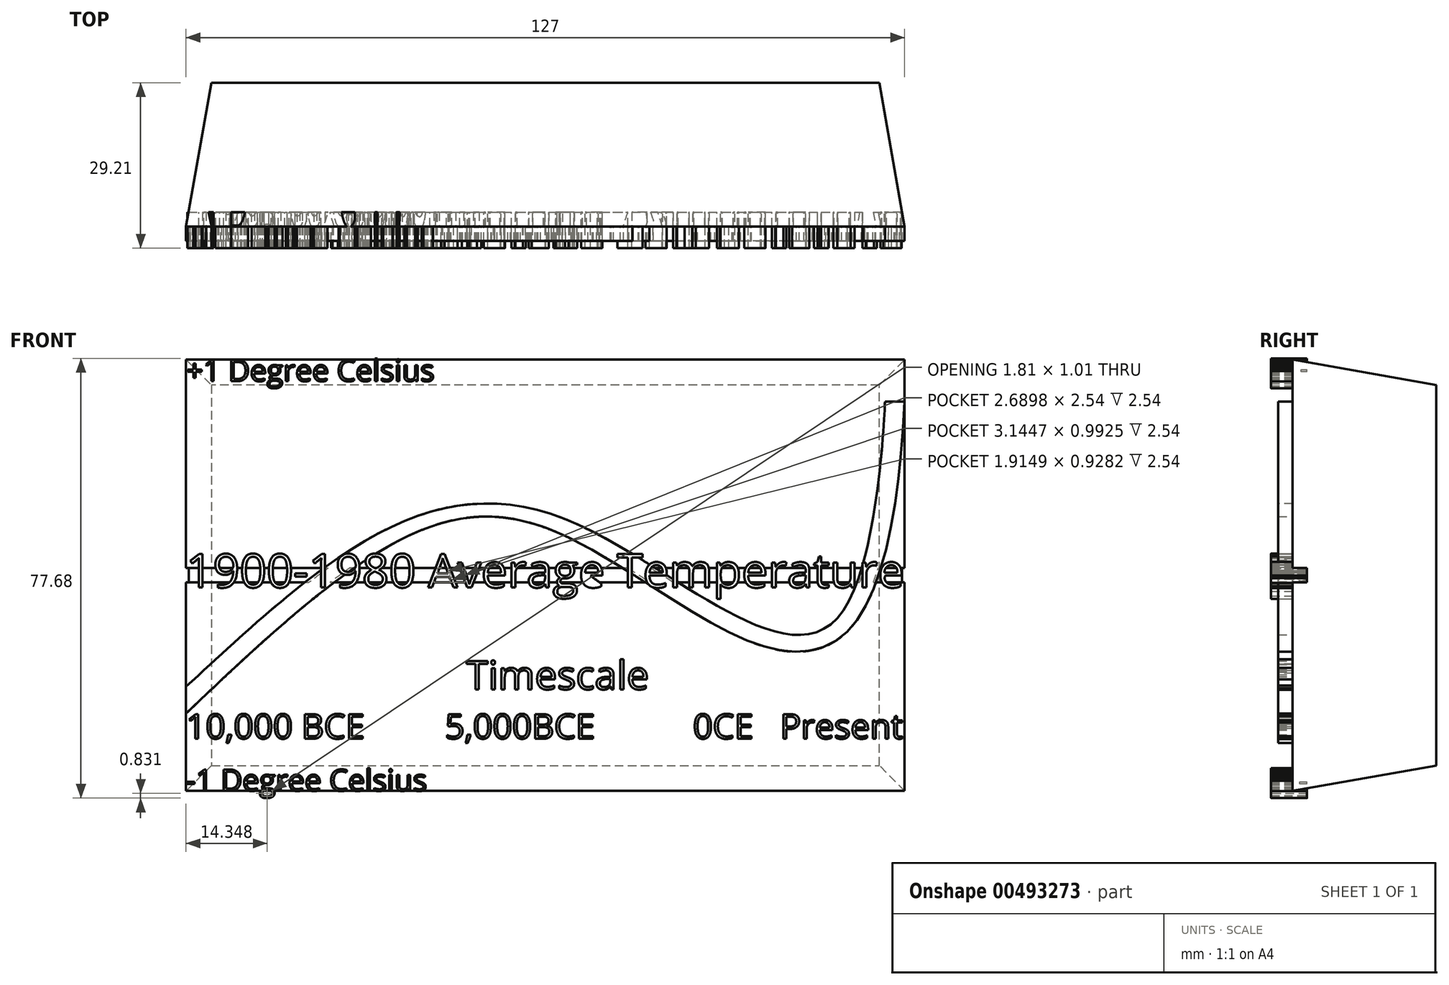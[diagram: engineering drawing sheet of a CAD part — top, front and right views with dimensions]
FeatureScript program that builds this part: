
annotation { "Feature Type Name" : "Feature", "Feature Type Description" : "" }
export const myFeature = defineFeature(function(context is Context, id is Id, definition is map)
    precondition{}
    {
        {
            var Q0;
            Q0=qCreatedBy(makeId("Front.planeOp"),FACE);
            var sketch = newSketch(context, id + "F0", { "sketchPlane" : qUnion([Q0])});
            skLineSegment(sketch, "E0.bottom", {"start": v(-127, 76.2) * mm, "end": v(0, 76.2) * mm});
            skLineSegment(sketch, "E0.top", {"start": v(-127, 0) * mm, "end": v(0, 0) * mm});
            skLineSegment(sketch, "E0.left", {"start": v(-127, 76.2) * mm, "end": v(-127, 0) * mm});
            skLineSegment(sketch, "E0.right", {"start": v(0, 76.2) * mm, "end": v(0, 0) * mm});
            skSolve(sketch);
        }
        {
            var Q0;
            Q0 = qSketchRegion(id + "F0", true);
            extrude(context, id + "F1", {"entities" : qUnion([Q0]), "oppositeDirection" : true, "depth" : 25.4 * mm, "hasDraft" : true, "draftAngle" : 10 * degree, "draftPullDirection" : true});
        }
        {
            var Q0;
            Q0=makeQuery(id+"F1.opExtrude","CAP_FACE",FACE,{"disambiguationData":[OSD([sQuery(id+"F0.wireOp",EDGE,"E0.bottom"),sQuery(id+"F0.wireOp",EDGE,"E0.top"),sQuery(id+"F0.wireOp",EDGE,"E0.left"),sQuery(id+"F0.wireOp",EDGE,"E0.right")])],"isStart":true});
            var sketch = newSketch(context, id + "F2", { "sketchPlane" : qUnion([Q0])});
            skLineSegment(sketch, "E1.bottom", {"start": v(-127, 39.37) * mm, "end": v(0, 39.37) * mm});
            skLineSegment(sketch, "E1.top", {"start": v(-127, 36.83) * mm, "end": v(0, 36.83) * mm});
            skLineSegment(sketch, "E1.left", {"start": v(-127, 39.37) * mm, "end": v(-127, 36.83) * mm});
            skLineSegment(sketch, "E1.right", {"start": v(0, 39.37) * mm, "end": v(0, 36.83) * mm});
            skSolve(sketch);
        }
        {
            var Q0;
            Q0 = qSketchRegion(id + "F2", true);
            extrude(context, id + "F3", {"entities" : qUnion([Q0]), "operationType" : NewBodyOperationType.REMOVE, "oppositeDirection" : true, "depth" : 2.54 * mm});
        }
        {
            var Q0;
            {var subQ0=sQuery(id+"F0.wireOp",EDGE,"E0.top");var subQ1=sQuery(id+"F0.wireOp",EDGE,"E0.left");var subQ2=sQuery(id+"F0.wireOp",EDGE,"E0.right");Q0=makeQuery(id+"F3.boolean.opBoolean","SPLIT",FACE,{"disambiguationData":[TD([makeQuery(id+"F1.opExtrude","SWEPT_FACE",FACE,{"disambiguationData":[OSD([subQ0])]})])],"derivedFrom":makeQuery(id+"F1.opExtrude","CAP_FACE",FACE,{"disambiguationData":[OSD([sQuery(id+"F0.wireOp",EDGE,"E0.bottom"),subQ0,subQ1,subQ2])],"isStart":true})});}
            var sketch = newSketch(context, id + "F4", { "sketchPlane" : qUnion([Q0])});
            skFitSpline(sketch, "E2", {"points": [v(-127, 20.22) * mm, v(-92.46, 43.91) * mm, v(-69.2, 46.48) * mm, v(-39.41, 27.82) * mm, v(-8.62, 29.1) * mm, v(0, 74.87) * mm], "startDerivative": vector(146.6, 137.46) * mm, "endDerivative": vector(6.88, 238.98) * mm});
            skLineSegment(sketch, "E3", {"start": v(-2.96, 74.87) * mm, "end": v(0, 74.87) * mm});
            skLineSegment(sketch, "E4", {"start": v(-127, 22.55) * mm, "end": v(-127, 20.22) * mm});
            skText(sketch, "E5", { "text": "+1 Degree Celsius", "fontName": "OpenSans-Regular.ttf"});
            skText(sketch, "E6", { "text": "-1 Degree Celsius", "fontName": "OpenSans-Regular.ttf"});
            skText(sketch, "E7", { "text": "1900-1980 Average Temperature", "fontName": "OpenSans-Regular.ttf"});
            const initialGuessF4  = {"E5": [-0.127, 0.07239, 1, 0, 0.00381], "E6": [-0.127, 0, 1, 0, 0.00381], "E7": [-0.127, 0.03594, 1, 0, 0.00597]};
            skSetInitialGuess(sketch, initialGuessF4);
            skSolve(sketch);
        }
        {
            var Q0;
            Q0 = qSketchRegion(id + "F4", true);
            extrude(context, id + "F5", {"entities" : qUnion([Q0]), "operationType" : NewBodyOperationType.ADD, "depth" : 3.8 * mm, "hasSecondDirection" : true, "secondDirectionOppositeDirection" : true, "secondDirectionDepth" : 2.54 * mm});
        }
        {
            var Q0;
            {var subQ193=sQuery(id+"F0.wireOp",EDGE,"E0.top");var subQ194=makeQuery(id+"F1.opExtrude","SWEPT_FACE",FACE,{"disambiguationData":[OSD([subQ193])]});var subQ197=sQuery(id+"F0.wireOp",EDGE,"E0.left");var subQ198=makeQuery(id+"F1.opExtrude","SWEPT_FACE",FACE,{"disambiguationData":[OSD([subQ197])]});var subQ203=sQuery(id+"F0.wireOp",EDGE,"E0.right");Q0=makeQuery(id+"F5.boolean.opBoolean","SPLIT",FACE,{"disambiguationData":[TD([subQ198])],"derivedFrom":makeQuery(id+"F3.boolean.opBoolean","SPLIT",FACE,{"disambiguationData":[TD([subQ194])],"derivedFrom":makeQuery(id+"F1.opExtrude","CAP_FACE",FACE,{"disambiguationData":[OSD([sQuery(id+"F0.wireOp",EDGE,"E0.bottom"),subQ193,subQ197,subQ203])],"isStart":true})})});}
            var sketch = newSketch(context, id + "F6", { "sketchPlane" : qUnion([Q0])});
            skFitSpline(sketch, "E8", {"points": [v(-127, 18.41) * mm, v(-90.16, 46.92) * mm, v(-62, 48.77) * mm, v(-29, 30.53) * mm, v(-10.52, 32.38) * mm, v(-3.49, 68.81) * mm], "startDerivative": vector(159.63, 147.7) * mm, "endDerivative": vector(0, 6.42) * mm});
            skFitSpline(sketch, "E9", {"points": [v(0, 68.81) * mm, v(-9.71, 28.63) * mm, v(-26.89, 26.2) * mm, v(-62.57, 46.16) * mm, v(-88.12, 44.87) * mm, v(-127, 13.7) * mm], "startDerivative": vector(-11.1, -223.46) * mm, "endDerivative": vector(-165.74, -157.7) * mm});
            skLineSegment(sketch, "E10", {"start": v(-127, 18.41) * mm, "end": v(-127, 13.7) * mm});
            skLineSegment(sketch, "E11", {"start": v(-3.49, 68.81) * mm, "end": v(0, 68.81) * mm});
            skSolve(sketch);
        }
        {
            var Q0;
            Q0 = qSketchRegion(id + "F6", true);
            var Q1;
            Q1=makeQuery(id+"F3.boolean.opBoolean","COPY",FACE,{"derivedFrom":makeQuery(id+"F3.opExtrude","CAP_FACE",FACE,{"disambiguationData":[OSD([sQuery(id+"F2.wireOp",EDGE,"E1.bottom"),sQuery(id+"F2.wireOp",EDGE,"E1.top"),sQuery(id+"F2.wireOp",EDGE,"E1.left"),sQuery(id+"F2.wireOp",EDGE,"E1.right")])],"isStart":false})});
            extrude(context, id + "F7", {"entities" : qUnion([Q0]), "operationType" : NewBodyOperationType.ADD, "depth" : 2.54 * mm, "hasSecondDirection" : true, "secondDirectionBound" : SecondDirectionBoundingType.UP_TO_SURFACE, "secondDirectionOppositeDirection" : true, "secondDirectionBoundEntityFace" : qUnion([Q1]), "secondDirectionDepth" : 25.4 * mm, "hasSecondDirectionDraft" : true, "secondDirectionDraftAngle" : 10 * degree, "secondDirectionDraftPullDirection" : true});
        }
        {
            var Q0;
            {var subQ171=sQuery(id+"F0.wireOp",EDGE,"E0.top");var subQ172=makeQuery(id+"F1.opExtrude","SWEPT_FACE",FACE,{"disambiguationData":[OSD([subQ171])]});var subQ183=sQuery(id+"F0.wireOp",EDGE,"E0.left");var subQ184=makeQuery(id+"F1.opExtrude","SWEPT_FACE",FACE,{"disambiguationData":[OSD([subQ183])]});var subQ196=sQuery(id+"F0.wireOp",EDGE,"E0.right");Q0=makeQuery(id+"F7.boolean.opBoolean","SPLIT",FACE,{"disambiguationData":[TD([subQ172])],"derivedFrom":makeQuery(id+"F5.boolean.opBoolean","SPLIT",FACE,{"disambiguationData":[TD([subQ184])],"derivedFrom":makeQuery(id+"F3.boolean.opBoolean","SPLIT",FACE,{"disambiguationData":[TD([subQ172])],"derivedFrom":makeQuery(id+"F1.opExtrude","CAP_FACE",FACE,{"disambiguationData":[OSD([sQuery(id+"F0.wireOp",EDGE,"E0.bottom"),subQ171,subQ183,subQ196])],"isStart":true})})})});}
            var sketch = newSketch(context, id + "F8", { "sketchPlane" : qUnion([Q0])});
            skText(sketch, "E12", { "text": "10,000 BCE         5,000BCE           0CE   Present", "fontName": "OpenSans-Regular.ttf"});
            skText(sketch, "E13", { "text": "Timescale", "fontName": "OpenSans-Regular.ttf"});
            const initialGuessF8  = {"E12": [-0.127, 0.00924, 1, 0, 0.00437], "E13": [-0.07748, 0.01795, 1, 0, 0.00503]};
            skSetInitialGuess(sketch, initialGuessF8);
            skSolve(sketch);
        }
        {
            var Q0;
            Q0 = qSketchRegion(id + "F8", true);
            extrude(context, id + "F9", {"entities" : qUnion([Q0]), "operationType" : NewBodyOperationType.ADD, "depth" : 2.54 * mm});
        }
    });
